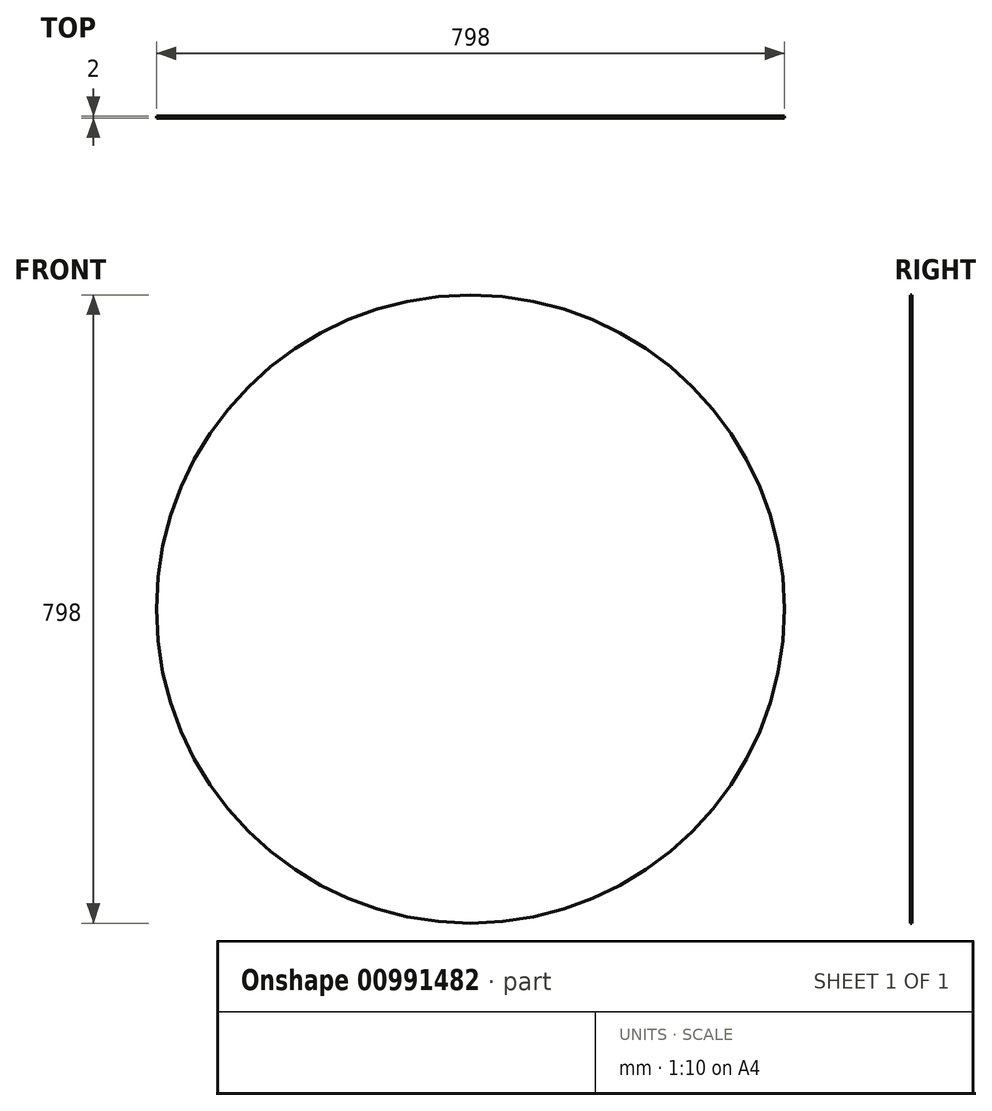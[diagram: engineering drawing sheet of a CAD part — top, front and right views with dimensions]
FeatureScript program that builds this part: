
annotation { "Feature Type Name" : "Feature", "Feature Type Description" : "" }
export const myFeature = defineFeature(function(context is Context, id is Id, definition is map)
    precondition{}
    {
        {
            var Q0;
            Q0=qCreatedBy(makeId("Front.planeOp"),FACE);
            var sketch = newSketch(context, id + "F0", { "sketchPlane" : qUnion([Q0])});
            skCircle(sketch, "E0", {"center": v(0, 0) * mm, "radius": 399 * mm});
            skSolve(sketch);
        }
        {
            var Q0;
            Q0=makeQuery(id+"F0.imprint","IMPRINT",FACE,{"disambiguationData":[TD([[makeQuery(id+"F0.imprint","IMPRINT",EDGE,{"derivedFrom":sQuery(id+"F0.wireOp",EDGE,"E0")}),1.0]])]});
            extrude(context, id + "F1", {"entities" : qUnion([Q0]), "depth" : 2 * mm, "offsetDistance" : 25 * mm});
        }
    });
